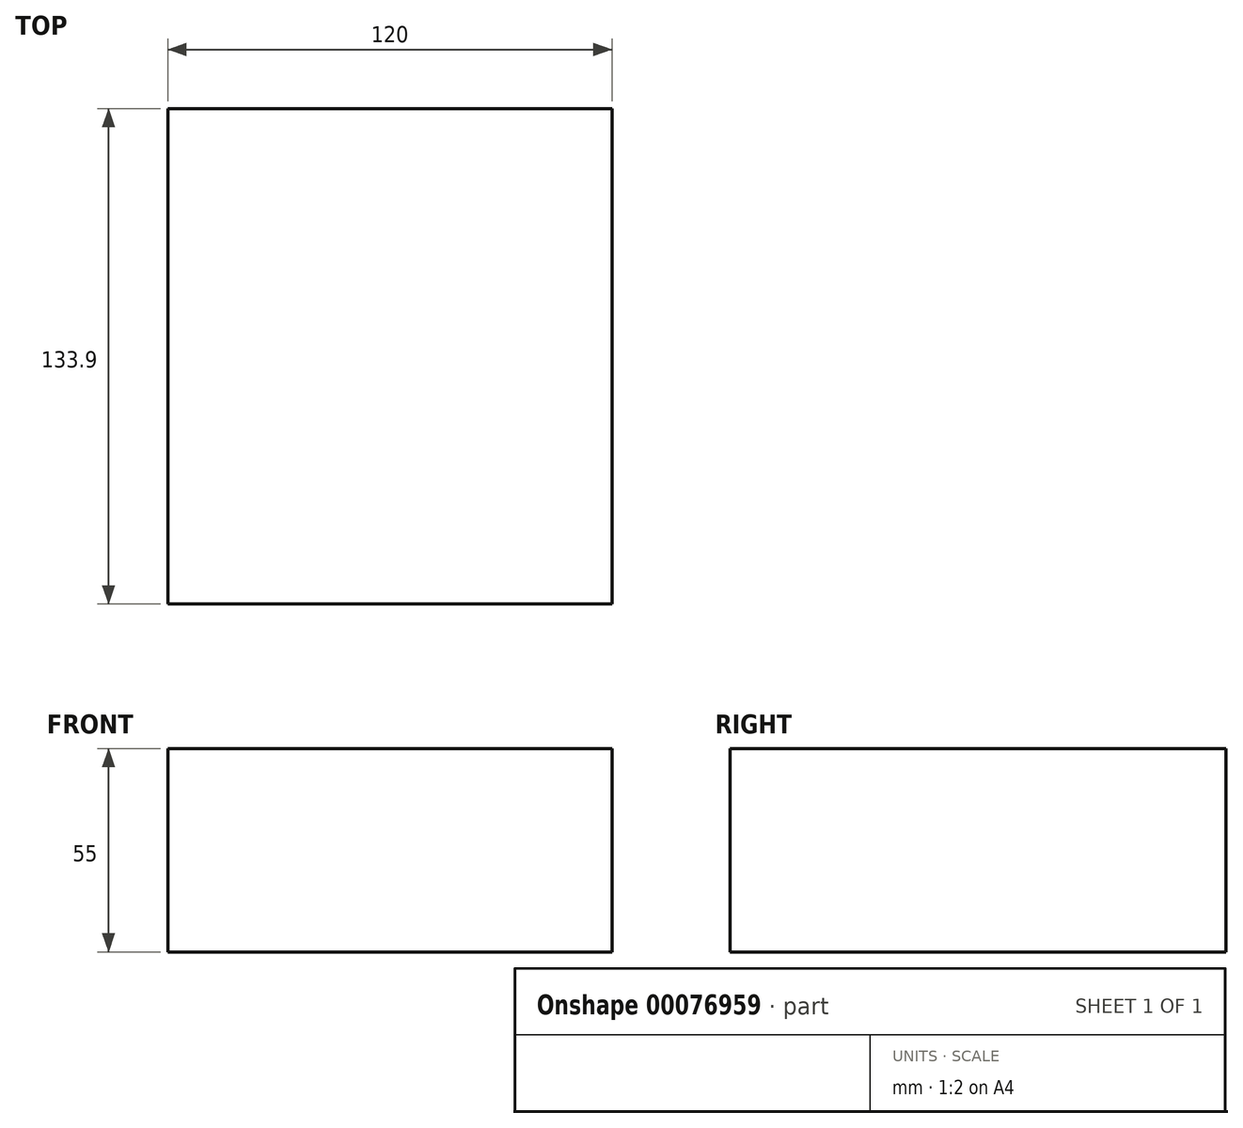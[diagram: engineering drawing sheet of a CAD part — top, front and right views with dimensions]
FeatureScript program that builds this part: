
annotation { "Feature Type Name" : "Feature", "Feature Type Description" : "" }
export const myFeature = defineFeature(function(context is Context, id is Id, definition is map)
    precondition{}
    {
        {
            var Q0;
            Q0=qCreatedBy(makeId("Front.planeOp"),FACE);
            var sketch = newSketch(context, id + "F0", { "sketchPlane" : qUnion([Q0])});
            skLineSegment(sketch, "E0.bottom", {"start": v(-60, 27.5) * mm, "end": v(60, 27.5) * mm});
            skLineSegment(sketch, "E0.top", {"start": v(-60, -27.5) * mm, "end": v(60, -27.5) * mm});
            skLineSegment(sketch, "E0.left", {"start": v(-60, 27.5) * mm, "end": v(-60, -27.5) * mm});
            skLineSegment(sketch, "E0.right", {"start": v(60, 27.5) * mm, "end": v(60, -27.5) * mm});
            skPoint(sketch, "E0.middle", {"position": v(0, 0) * mm});
            skSolve(sketch);
        }
        {
            var Q0;
            Q0=makeQuery(id+"F0.imprint","IMPRINT",FACE,{"disambiguationData":[TD([[makeQuery(id+"F0.imprint","IMPRINT",EDGE,{"derivedFrom":sQuery(id+"F0.wireOp",EDGE,"E0.bottom")}),-1.0]])]});
            extrude(context, id + "F1", {"entities" : qUnion([Q0]), "depth" : 133.9 * mm});
        }
    });
